# Revit family: Kabelrinne_650_FT_FS_FTSO_A2_A4
name_source: partatom
category: Generic Models
revit_build: Autodesk Revit 2017 (Build: 20160225_1515(x64)
units: mm (PartAtom-declared; Revit-internal decimal feet)

## family parameters
Always vertical = Yes
Can host rebar = No
Cut with Voids When Loaded = No
Part Type = Normal
Room Calculation Point = No
Round Connector Dimension = Use Diameter
Shared = No
Work Plane-Based = No

## types (6) — shared parameters
Cut's number = 2
Cut's number 2 = 60
Cut's number 3 = 59
Cut's space = 50 mm  [stored 0.164042 ft]
Height = 51 mm
Length = 3000 mm  [stored 9.84252 ft]
Manufacturer = OBO BETTERMANN
URL = http:/www.obo-bettermann.com

## per-type parameters (varying)
| type | Article Type | GTIN | Manufacturer Art.No. | Material | Width | Width 1 |
| SKS 650 FT | SKS 650 FT | 4012196060610 | 6056717 | hot-dip galvanised | 500 mm  [stored 1.64042 ft] | 250 mm  [stored 0.82021 ft] |
| SKS 650 A2 | SKS 650 A2 | 4012196120796 | 6056744 | Stainless steel A4 | 500 mm  [stored 1.64042 ft] | 250 mm  [stored 0.82021 ft] |
| SKS 650 A4 | SKS 650 A4 | 4012196050406 | 6056761 | Stainless steel A4 | 500 mm  [stored 1.64042 ft] | 250 mm  [stored 0.82021 ft] |
| SKS 640 FS | SKS 640 FT SO | 4012196014897 | 7190158 | hot-dip galvanised | 400 mm  [stored 1.31234 ft] | 200 mm  [stored 0.656168 ft] |
| SKS 650 FT SO | SKS 650 FT SO | 4012195020745 | 7190167 | hot-dip galvanised | 500 mm  [stored 1.64042 ft] | 250 mm  [stored 0.82021 ft] |
| SKS 650 FS | SKS 650 FS | 4012196060436 | 6056504 | Polyester/Epoxid/Korrosionschutz | 500 mm  [stored 1.64042 ft] | 250 mm  [stored 0.82021 ft] |

note: [stored X ft] marks values corroborated as IEEE doubles in the binary element streams (Revit-internal decimal feet)

## geometry (parser evidence)
native form markers: Sweep x2
no freeform markers — native parametric forms only
